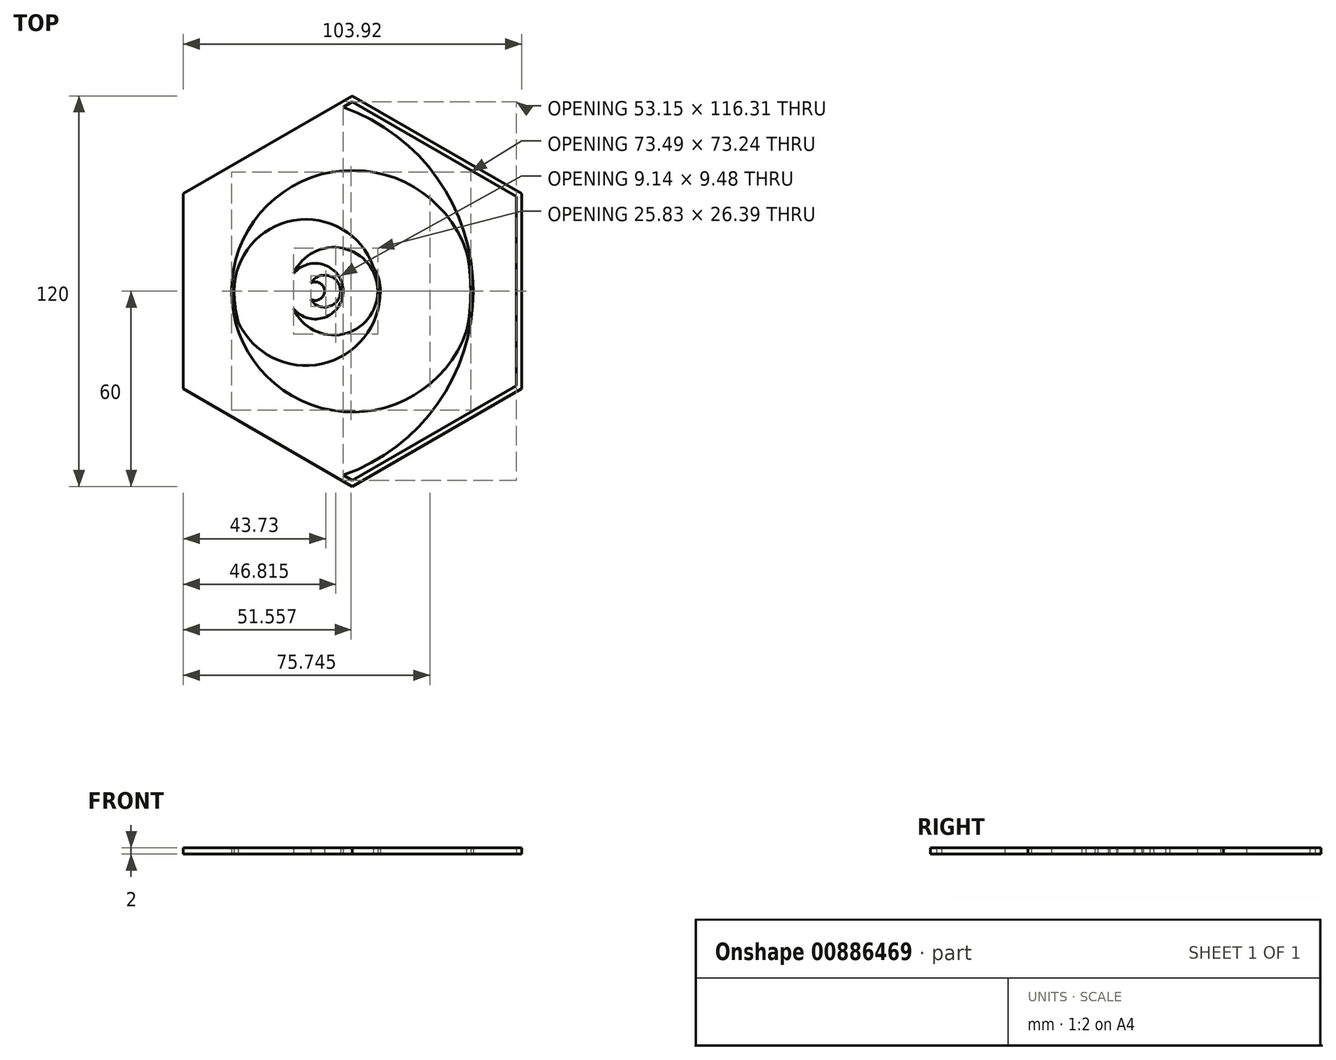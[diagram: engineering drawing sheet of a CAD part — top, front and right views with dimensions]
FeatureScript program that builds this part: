
annotation { "Feature Type Name" : "Feature", "Feature Type Description" : "" }
export const myFeature = defineFeature(function(context is Context, id is Id, definition is map)
    precondition{}
    {
        {
            var Q0;
            Q0=qCreatedBy(makeId("Top.planeOp"),FACE);
            var sketch = newSketch(context, id + "F0", { "sketchPlane" : qUnion([Q0])});
            skArc(sketch, "E0", {"start": v(41.43, 32.17) * mm, "mid": v(-14.29, 0) * mm, "end": v(41.43, -32.17) * mm});
            skCircle(sketch, "E1", {"center": v(8.57, 0) * mm, "radius": 22.86 * mm});
            skCircle(sketch, "E2", {"center": v(17.14, 0) * mm, "radius": 14.29 * mm});
            skCircle(sketch, "E3", {"center": v(11.43, 0) * mm, "radius": 8.57 * mm});
            skCircle(sketch, "E4", {"center": v(14.29, 0) * mm, "radius": 5.71 * mm});
            skArc(sketch, "E5.0", {"start": v(42.26, 30.73) * mm, "mid": v(-13.49, 0) * mm, "end": v(42.26, -30.73) * mm});
            skCircle(sketch, "E6.0", {"center": v(8.57, 0) * mm, "radius": 22.06 * mm});
            skCircle(sketch, "E7.0", {"center": v(17.14, 0) * mm, "radius": 13.49 * mm});
            skCircle(sketch, "E8.0", {"center": v(11.43, 0) * mm, "radius": 7.77 * mm});
            skCircle(sketch, "E9.0", {"center": v(14.29, 0) * mm, "radius": 4.91 * mm});
            skArc(sketch, "E10.trimOffspring", {"start": v(59.17, -1.43) * mm, "mid": v(59.2, 0) * mm, "end": v(59.17, 1.43) * mm});
            skCircle(sketch, "E11", {"center": v(22.86, 0) * mm, "radius": 36.34 * mm});
            skCircle(sketch, "E12", {"center": v(22.86, 0) * mm, "radius": 37.14 * mm});
            skCircle(sketch, "E13", {"center": v(11.43, 0) * mm, "radius": 2.86 * mm});
            skCircle(sketch, "E14.0", {"center": v(11.43, 0) * mm, "radius": 2.06 * mm});
            skCircle(sketch, "E15.cCircle", {"center": v(22.86, 0) * mm, "radius": 60 * mm, "construction": true});
            skLineSegment(sketch, "E15.0", {"start": v(-29.1, 30) * mm, "end": v(22.86, 60) * mm});
            skLineSegment(sketch, "E15.1", {"start": v(22.86, 60) * mm, "end": v(74.82, 30) * mm});
            skLineSegment(sketch, "E15.2", {"start": v(74.82, 30) * mm, "end": v(74.82, -30) * mm});
            skLineSegment(sketch, "E15.3", {"start": v(74.82, -30) * mm, "end": v(22.86, -60) * mm});
            skLineSegment(sketch, "E15.4", {"start": v(22.86, -60) * mm, "end": v(-29.1, -30) * mm});
            skLineSegment(sketch, "E15.5", {"start": v(-29.1, -30) * mm, "end": v(-29.1, 30) * mm});
            skArc(sketch, "E16", {"start": v(18.05, -57.22) * mm, "mid": v(60, 0) * mm, "end": v(18.05, 57.22) * mm});
            skArc(sketch, "E17.0", {"start": v(17.1, -56.68) * mm, "mid": v(59.2, 0) * mm, "end": v(17.1, 56.68) * mm});
            skLineSegment(sketch, "E18.0", {"start": v(-27.5, -29.08) * mm, "end": v(-27.5, 29.08) * mm});
            skLineSegment(sketch, "E18.1", {"start": v(22.86, 58.15) * mm, "end": v(73.22, 29.08) * mm});
            skLineSegment(sketch, "E18.2", {"start": v(73.22, 29.08) * mm, "end": v(73.22, -29.08) * mm});
            skLineSegment(sketch, "E18.3", {"start": v(-27.5, 29.08) * mm, "end": v(22.86, 58.15) * mm});
            skLineSegment(sketch, "E18.4", {"start": v(73.22, -29.08) * mm, "end": v(22.86, -58.15) * mm});
            skLineSegment(sketch, "E18.5", {"start": v(22.86, -58.15) * mm, "end": v(-27.5, -29.08) * mm});
            skSolve(sketch);
        }
        {
            var Q0;
            Q0=makeQuery(id+"F0.imprint","IMPRINT",FACE,{"disambiguationData":[TD([[makeQuery(id+"F0.imprint","IMPRINT",EDGE,{"derivedFrom":sQuery(id+"F0.wireOp",EDGE,"E14.0")}),1.0]])]});
            var Q1;
            {var subQ0=sQuery(id+"F0.wireOp",EDGE,"E14.0");Q1=makeQuery(id+"F0.imprint","IMPRINT",FACE,{"disambiguationData":[TD([[makeQuery(id+"F0.imprint","IMPRINT",EDGE,{"derivedFrom":subQ0}),-1.0]])]});}
            var Q2;
            {var subQ0=sQuery(id+"F0.wireOp",EDGE,"E8.0");var subQ1=sQuery(id+"F0.wireOp",EDGE,"E4");var subQ2=makeQuery(id+"F0.imprint","INTERSECT",VERTEX,{"disambiguationData":[OD(0.0)],"derivedFrom":[subQ1,subQ0]});Q2=makeQuery(id+"F0.imprint","IMPRINT",FACE,{"disambiguationData":[TD([[makeQuery(id+"F0.imprint","IMPRINT",EDGE,{"disambiguationData":[TD([[subQ2,-1.0]])],"derivedFrom":subQ1}),1.0]])]});}
            var Q3;
            {var subQ0=sQuery(id+"F0.wireOp",EDGE,"E9.0");var subQ1=makeQuery(id+"F0.imprint","INTERSECT",VERTEX,{"derivedFrom":[subQ0,sQuery(id+"F0.wireOp",EDGE,"E14.0")]});Q3=makeQuery(id+"F0.imprint","IMPRINT",FACE,{"disambiguationData":[TD([[makeQuery(id+"F0.imprint","IMPRINT",EDGE,{"disambiguationData":[TD([[subQ1,1.0]])],"derivedFrom":subQ0}),-1.0]])]});}
            var Q4;
            {var subQ0=sQuery(id+"F0.wireOp",EDGE,"E13");var subQ1=sQuery(id+"F0.wireOp",EDGE,"E4");var subQ2=makeQuery(id+"F0.imprint","INTERSECT",VERTEX,{"derivedFrom":[subQ1,subQ0]});Q4=makeQuery(id+"F0.imprint","IMPRINT",FACE,{"disambiguationData":[TD([[makeQuery(id+"F0.imprint","IMPRINT",EDGE,{"disambiguationData":[TD([[subQ2,-1.0]])],"derivedFrom":subQ1}),1.0]])]});}
            var Q5;
            {var subQ0=sQuery(id+"F0.wireOp",EDGE,"E8.0");var subQ1=sQuery(id+"F0.wireOp",EDGE,"E4");var subQ2=makeQuery(id+"F0.imprint","INTERSECT",VERTEX,{"disambiguationData":[OD(0.0)],"derivedFrom":[subQ1,subQ0]});Q5=makeQuery(id+"F0.imprint","IMPRINT",FACE,{"disambiguationData":[TD([[makeQuery(id+"F0.imprint","IMPRINT",EDGE,{"disambiguationData":[TD([[subQ2,-1.0]])],"derivedFrom":subQ1}),-1.0]])]});}
            var Q6;
            {var subQ0=sQuery(id+"F0.wireOp",EDGE,"E7.0");var subQ1=sQuery(id+"F0.wireOp",EDGE,"E3");var subQ2=makeQuery(id+"F0.imprint","INTERSECT",VERTEX,{"disambiguationData":[OD(0.0)],"derivedFrom":[subQ1,subQ0]});Q6=makeQuery(id+"F0.imprint","IMPRINT",FACE,{"disambiguationData":[TD([[makeQuery(id+"F0.imprint","IMPRINT",EDGE,{"disambiguationData":[TD([[subQ2,1.0]])],"derivedFrom":subQ1}),1.0]])]});}
            var Q7;
            {var subQ0=sQuery(id+"F0.wireOp",EDGE,"E3");var subQ1=makeQuery(id+"F0.imprint","INTERSECT",VERTEX,{"derivedFrom":[sQuery(id+"F0.wireOp",EDGE,"E2"),subQ0]});Q7=makeQuery(id+"F0.imprint","IMPRINT",FACE,{"disambiguationData":[TD([[makeQuery(id+"F0.imprint","IMPRINT",EDGE,{"disambiguationData":[TD([[subQ1,1.0]])],"derivedFrom":subQ0}),1.0]])]});}
            var Q8;
            {var subQ0=sQuery(id+"F0.wireOp",EDGE,"E6.0");var subQ1=sQuery(id+"F0.wireOp",EDGE,"E2");var subQ2=makeQuery(id+"F0.imprint","INTERSECT",VERTEX,{"disambiguationData":[OD(0.0)],"derivedFrom":[subQ1,subQ0]});Q8=makeQuery(id+"F0.imprint","IMPRINT",FACE,{"disambiguationData":[TD([[makeQuery(id+"F0.imprint","IMPRINT",EDGE,{"disambiguationData":[TD([[subQ2,-1.0]])],"derivedFrom":subQ1}),1.0]])]});}
            var Q9;
            {var subQ0=sQuery(id+"F0.wireOp",EDGE,"E3");var subQ1=sQuery(id+"F0.wireOp",EDGE,"E2");var subQ2=makeQuery(id+"F0.imprint","INTERSECT",VERTEX,{"derivedFrom":[subQ1,subQ0]});Q9=makeQuery(id+"F0.imprint","IMPRINT",FACE,{"disambiguationData":[TD([[makeQuery(id+"F0.imprint","IMPRINT",EDGE,{"disambiguationData":[TD([[subQ2,-1.0]])],"derivedFrom":subQ1}),1.0]])]});}
            var Q10;
            {var subQ0=sQuery(id+"F0.wireOp",EDGE,"E6.0");var subQ1=sQuery(id+"F0.wireOp",EDGE,"E2");var subQ2=makeQuery(id+"F0.imprint","INTERSECT",VERTEX,{"disambiguationData":[OD(0.0)],"derivedFrom":[subQ1,subQ0]});Q10=makeQuery(id+"F0.imprint","IMPRINT",FACE,{"disambiguationData":[TD([[makeQuery(id+"F0.imprint","IMPRINT",EDGE,{"disambiguationData":[TD([[subQ2,-1.0]])],"derivedFrom":subQ1}),-1.0]])]});}
            var Q11;
            {var subQ0=sQuery(id+"F0.wireOp",EDGE,"E11");var subQ1=sQuery(id+"F0.wireOp",EDGE,"E1");var subQ2=makeQuery(id+"F0.imprint","INTERSECT",VERTEX,{"disambiguationData":[OD(0.0)],"derivedFrom":[subQ1,subQ0]});Q11=makeQuery(id+"F0.imprint","IMPRINT",FACE,{"disambiguationData":[TD([[makeQuery(id+"F0.imprint","IMPRINT",EDGE,{"disambiguationData":[TD([[subQ2,1.0]])],"derivedFrom":subQ1}),1.0]])]});}
            var Q12;
            {var subQ0=sQuery(id+"F0.wireOp",EDGE,"E11");var subQ1=sQuery(id+"F0.wireOp",EDGE,"E1");var subQ2=makeQuery(id+"F0.imprint","INTERSECT",VERTEX,{"disambiguationData":[OD(0.0)],"derivedFrom":[subQ1,subQ0]});Q12=makeQuery(id+"F0.imprint","IMPRINT",FACE,{"disambiguationData":[TD([[makeQuery(id+"F0.imprint","IMPRINT",EDGE,{"disambiguationData":[TD([[subQ2,-1.0]])],"derivedFrom":subQ1}),1.0]])]});}
            var Q13;
            {var subQ0=sQuery(id+"F0.wireOp",EDGE,"E11");var subQ9=makeQuery(id+"F0.imprint","IMPRINT",VERTEX,{"disambiguationData":[OD(0.0)],"derivedFrom":subQ0});Q13=makeQuery(id+"F0.imprint","IMPRINT",FACE,{"disambiguationData":[TD([[makeQuery(id+"F0.imprint","IMPRINT",EDGE,{"disambiguationData":[TD([[subQ9,-1.0]])],"derivedFrom":subQ0}),-1.0]])]});}
            var Q14;
            {var subQ0=sQuery(id+"F0.wireOp",EDGE,"E2");var subQ1=sQuery(id+"F0.wireOp",EDGE,"E1");var subQ2=makeQuery(id+"F0.imprint","INTERSECT",VERTEX,{"derivedFrom":[subQ1,subQ0]});Q14=makeQuery(id+"F0.imprint","IMPRINT",FACE,{"disambiguationData":[TD([[makeQuery(id+"F0.imprint","IMPRINT",EDGE,{"disambiguationData":[TD([[subQ2,1.0]])],"derivedFrom":subQ1}),1.0]])]});}
            var Q15;
            {var subQ0=sQuery(id+"F0.wireOp",EDGE,"E11");var subQ4=makeQuery(id+"F0.imprint","IMPRINT",VERTEX,{"disambiguationData":[OD(2.0)],"derivedFrom":subQ0});Q15=makeQuery(id+"F0.imprint","IMPRINT",FACE,{"disambiguationData":[TD([[makeQuery(id+"F0.imprint","IMPRINT",EDGE,{"disambiguationData":[TD([[subQ4,-1.0]])],"derivedFrom":subQ0}),-1.0]])]});}
            var Q16;
            {var subQ11=sQuery(id+"F0.wireOp",EDGE,"E18.0");Q16=makeQuery(id+"F0.imprint","IMPRINT",FACE,{"disambiguationData":[TD([[makeQuery(id+"F0.imprint","IMPRINT",EDGE,{"derivedFrom":subQ11}),-1.0]])]});}
            var Q17;
            {var subQ5=sQuery(id+"F0.wireOp",EDGE,"E15.5");Q17=makeQuery(id+"F0.imprint","IMPRINT",FACE,{"disambiguationData":[TD([[makeQuery(id+"F0.imprint","IMPRINT",EDGE,{"derivedFrom":subQ5}),-1.0]])]});}
            var Q18;
            {var subQ0=sQuery(id+"F0.wireOp",EDGE,"E17.0");var subQ1=sQuery(id+"F0.wireOp",EDGE,"E12");var subQ2=makeQuery(id+"F0.imprint","INTERSECT",VERTEX,{"disambiguationData":[OD(0.0)],"derivedFrom":[subQ1,subQ0]});Q18=makeQuery(id+"F0.imprint","IMPRINT",FACE,{"disambiguationData":[TD([[makeQuery(id+"F0.imprint","IMPRINT",EDGE,{"disambiguationData":[TD([[subQ2,1.0]])],"derivedFrom":subQ1}),1.0]])]});}
            var Q19;
            {var subQ0=sQuery(id+"F0.wireOp",EDGE,"E17.0");var subQ1=sQuery(id+"F0.wireOp",EDGE,"E12");var subQ2=makeQuery(id+"F0.imprint","INTERSECT",VERTEX,{"disambiguationData":[OD(0.0)],"derivedFrom":[subQ1,subQ0]});Q19=makeQuery(id+"F0.imprint","IMPRINT",FACE,{"disambiguationData":[TD([[makeQuery(id+"F0.imprint","IMPRINT",EDGE,{"disambiguationData":[TD([[subQ2,1.0]])],"derivedFrom":subQ1}),-1.0]])]});}
            var Q20;
            {var subQ11=sQuery(id+"F0.wireOp",EDGE,"E15.1");Q20=makeQuery(id+"F0.imprint","IMPRINT",FACE,{"disambiguationData":[TD([[makeQuery(id+"F0.imprint","IMPRINT",EDGE,{"derivedFrom":subQ11}),-1.0]])]});}
            var Q21;
            {var subQ0=sQuery(id+"F0.wireOp",EDGE,"E16");var subQ1=sQuery(id+"F0.wireOp",EDGE,"E12");var subQ2=makeQuery(id+"F0.imprint","INTERSECT",VERTEX,{"derivedFrom":[subQ1,subQ0]});Q21=makeQuery(id+"F0.imprint","IMPRINT",FACE,{"disambiguationData":[TD([[makeQuery(id+"F0.imprint","IMPRINT",EDGE,{"disambiguationData":[TD([[subQ2,1.0]])],"derivedFrom":subQ1}),-1.0]])]});}
            var Q22;
            {var subQ0=sQuery(id+"F0.wireOp",EDGE,"E16");var subQ1=sQuery(id+"F0.wireOp",EDGE,"E15.4");var subQ2=makeQuery(id+"F0.imprint","INTERSECT",VERTEX,{"derivedFrom":[subQ1,subQ0]});Q22=makeQuery(id+"F0.imprint","IMPRINT",FACE,{"disambiguationData":[TD([[makeQuery(id+"F0.imprint","IMPRINT",EDGE,{"disambiguationData":[TD([[subQ2,-1.0]])],"derivedFrom":subQ1}),-1.0]])]});}
            var Q23;
            {var subQ0=sQuery(id+"F0.wireOp",EDGE,"E16");var subQ1=sQuery(id+"F0.wireOp",EDGE,"E15.0");var subQ2=makeQuery(id+"F0.imprint","INTERSECT",VERTEX,{"derivedFrom":[subQ1,subQ0]});Q23=makeQuery(id+"F0.imprint","IMPRINT",FACE,{"disambiguationData":[TD([[makeQuery(id+"F0.imprint","IMPRINT",EDGE,{"disambiguationData":[TD([[subQ2,1.0]])],"derivedFrom":subQ1}),-1.0]])]});}
            var Q24;
            {var subQ0=sQuery(id+"F0.wireOp",EDGE,"E2");var subQ1=makeQuery(id+"F0.imprint","INTERSECT",VERTEX,{"derivedFrom":[sQuery(id+"F0.wireOp",EDGE,"E1"),subQ0]});Q24=makeQuery(id+"F0.imprint","IMPRINT",FACE,{"disambiguationData":[TD([[makeQuery(id+"F0.imprint","IMPRINT",EDGE,{"disambiguationData":[TD([[subQ1,-1.0]])],"derivedFrom":subQ0}),1.0]])]});}
            var Q25;
            {var subQ0=sQuery(id+"F0.wireOp",EDGE,"E4");var subQ1=makeQuery(id+"F0.imprint","INTERSECT",VERTEX,{"derivedFrom":[sQuery(id+"F0.wireOp",EDGE,"E3"),subQ0]});Q25=makeQuery(id+"F0.imprint","IMPRINT",FACE,{"disambiguationData":[TD([[makeQuery(id+"F0.imprint","IMPRINT",EDGE,{"disambiguationData":[TD([[subQ1,-1.0]])],"derivedFrom":subQ0}),1.0]])]});}
            var Q26;
            {var subQ0=sQuery(id+"F0.wireOp",EDGE,"E4");var subQ1=sQuery(id+"F0.wireOp",EDGE,"E3");var subQ2=makeQuery(id+"F0.imprint","INTERSECT",VERTEX,{"derivedFrom":[subQ1,subQ0]});Q26=makeQuery(id+"F0.imprint","IMPRINT",FACE,{"disambiguationData":[TD([[makeQuery(id+"F0.imprint","IMPRINT",EDGE,{"disambiguationData":[TD([[subQ2,1.0]])],"derivedFrom":subQ1}),1.0]])]});}
            extrude(context, id + "F1", {"entities" : qUnion([Q0, Q1, Q2, Q3, Q4, Q5, Q6, Q7, Q8, Q9, Q10, Q11, Q12, Q13, Q14, Q15, Q16, Q17, Q18, Q19, Q20, Q21, Q22, Q23, Q24, Q25, Q26]), "depth" : 2 * mm, "offsetDistance" : 25 * mm});
        }
    });
